# Revit family: conv_troax_wall_fencedoor_ux550
name_source: partatom
category: Sonderausstattung
revit_build: Autodesk Revit 2017 (Build: 20160225_1515(x64)
units: mm (PartAtom-declared; Revit-internal decimal feet)

## family parameters
Arbeitsebenenbasiert = Nein
Beim Laden mit Abzugskörper schneiden = Nein
Bemaßung runder Anschluss = Durchmesser verwenden
Gemeinsam genutzt = Nein
Immer vertikal = Ja
OmniClass-Nummer = 23.25.40.21.21.11
OmniClass-Titel = Swinging Gates
Raumberechnungspunkt = Nein
Teiletyp = Normal

## types (1)
- Troax safe UX 550 cylinder
    AssetType = Fixed
    Beschreibung = The Troax Safe door is designed to be used with UX 550 mesh panel system and is suitable for storage areas in need of highest level of protection and is part of a system with specially adapted installation fittings. The System is used in areas which are particularly susceptible to break-in attempts. The door leaf has a 30x20 mm steel tube frame and two horizontal tubes to create strength and stability. The 50x50 mesh aperture also makes it virtually impossible for a hand to reach through the mesh. Doors are supplied preassembled, ready for installation.
    Brand = Troax
    Category = Doors
    Color = Grey
    Constituents = Single profile UX 550 L=2160; Join profile UX 550 L=2160; Corner profile UX 550 L=2160 outwards; Corner profile UX 550 L=2160 inwards; Wall profile UX 550 L=2160; Join profile UX 550 L=2160 cyl. door; Cable protection Door UX 550AC 900
    ConvergoRefNr = 0054-1811-0039-SE
    DoorType = Door UX550
    DurationUnit = Year
    Features = The door leaf has a 30x20 mm steel tube frame and two horizontal tubes to create strength and stability. The 50x50 mesh aperture also makes it virtually impossible for a hand to reach through the mesh. Doors are supplied preassembled, ready for installation.
    Finish = Powder coated as standard with a grey RAL 7037 finish. However other RAL colors are available upon request.
    FurniturePanelType = Other
    HasOpening = Ja
    Hersteller = Troax
    IfcExportAs = IfcSystemFurnitureElementTypePanel
    IfcExportType = DOOR
    Kosten = 0 $
    MainColor = Grey
    ManufacturerName = Troax
    ManufacturerURL = https://www.troax.com
    Material = Carbon steel
    Modell = Troax safe UX 550 cylinder
    NBSDescription = Metal doorsets
    NBSReference = 45-25-28/344
    Name = Wall_FenceDoor_UX550
    NominalDepth = 148 mm  [stored 0.485564 ft]
    NominalHeight = 2200 mm
    NominalThickness = 0 mm  [stored 0 ft]
    NominalWidth = 900 mm  [stored 2.95276 ft]
    ProductDatasheet = https://www.troax.com
    ProductInformation = The Troax Safe door is designed to be used with UX 550 mesh panel system and is suitable for storage areas in need of highest level of protection and is part of a system with specially adapted installation fittings.
    Shape = Sculptured
    Size = 148x2200x900 mm
    Uniclass2 = Pr_30_59_23_11
    Uniclass2015Description = Carbon steel door frames
    Uniclass2015Reference = Pr_30_59_23_11
    Version = 1
    VersionDate = 12/11/2018
    WallPanelMainMaterial = Steel, Carbon
    WarrantyDurationUnit = Year

note: [stored X ft] marks values corroborated as IEEE doubles in the binary element streams (Revit-internal decimal feet)

## geometry (parser evidence)
native form markers: Blend x4, Sweep x4
no freeform markers — native parametric forms only
